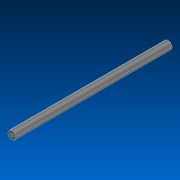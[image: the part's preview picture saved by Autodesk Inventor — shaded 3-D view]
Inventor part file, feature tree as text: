
AUTODESK INVENTOR PART (.ipt)
format: ipt  version: 2022.2 (Build 262287000, 287)  size: 121,856 bytes
history: native  units: in
note: dims shown in document units (in); Inventor stores cm internally (conversion verified against a paired STEP export)
features: extrude x1, sketch x1, other x1
ambient origin geometry x8: Origin, YZ Plane, XZ Plane, XY Plane, X Axis, Y Axis, Z Axis, Center Point
bodies: Solid1 (feature_tree)
feature tree (3):
  extrude  "Extrusion1"  TaperAngle=0.0deg  [1 undecoded]
  sketch  "Sketch1"  dims[d0=25.5in d1=0.0in]
  other  "Cut-Extrude2"
note: 1 required parameter value undecoded (feature->parameter linkage not recoverable at this tier; creation-order binding heuristic only, values carry confidence <= 0.55)
